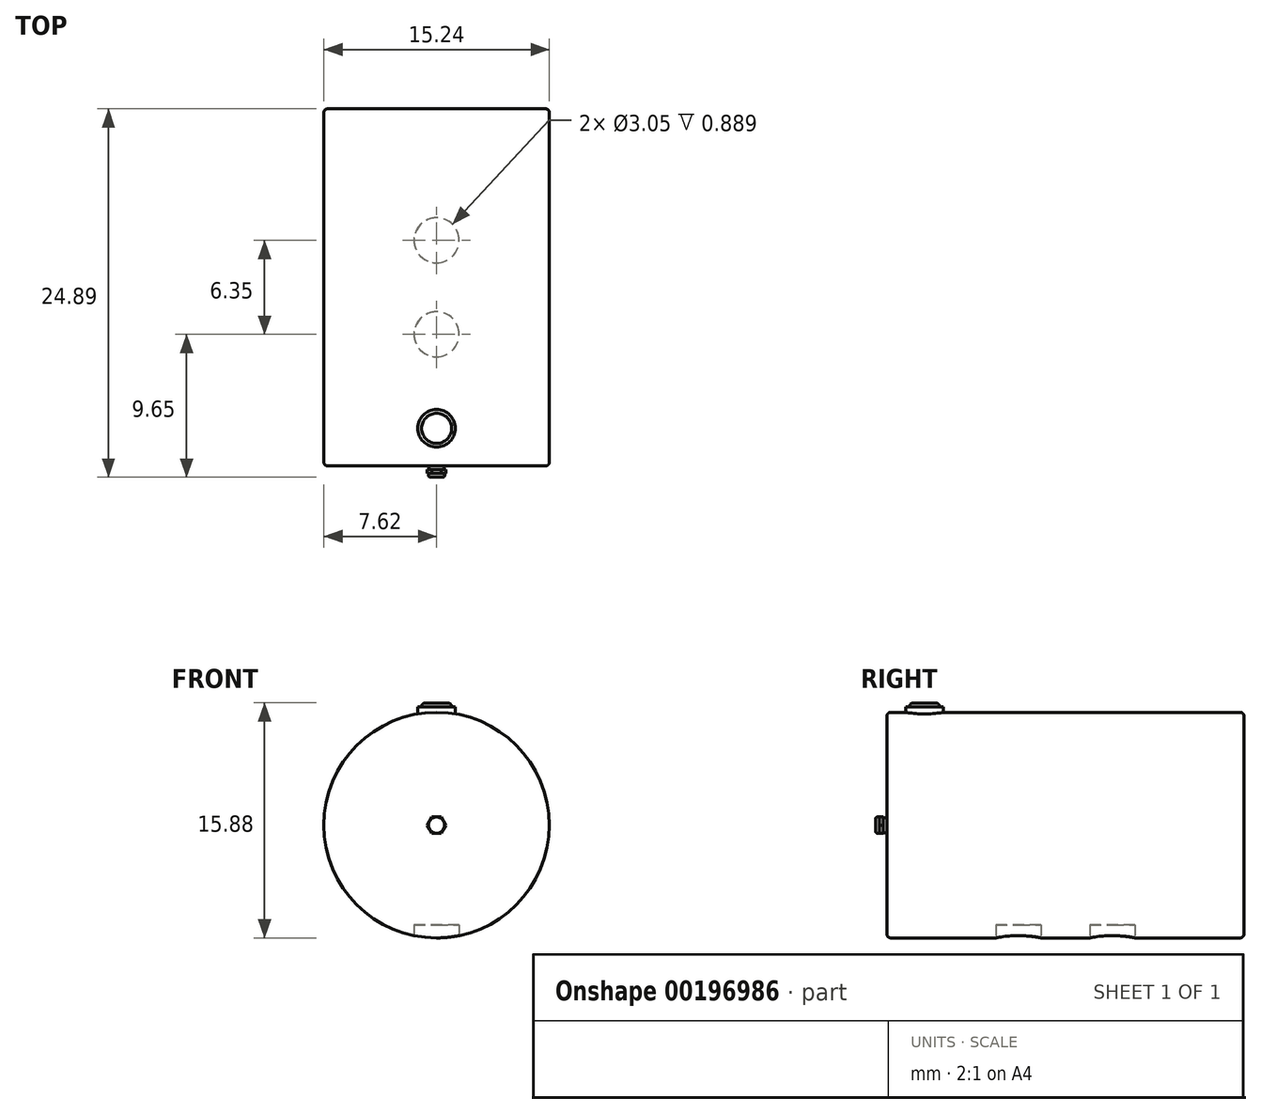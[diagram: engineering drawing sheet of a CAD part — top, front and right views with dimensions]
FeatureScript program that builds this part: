
annotation { "Feature Type Name" : "Feature", "Feature Type Description" : "" }
export const myFeature = defineFeature(function(context is Context, id is Id, definition is map)
    precondition{}
    {
        {
            var Q0;
            Q0=qCreatedBy(makeId("Front.planeOp"),FACE);
            var sketch = newSketch(context, id + "F0", { "sketchPlane" : qUnion([Q0])});
            skCircle(sketch, "E0", {"center": v(0, 0) * mm, "radius": 7.62 * mm});
            skSolve(sketch);
        }
        {
            var Q0;
            Q0 = qSketchRegion(id + "F0", true);
            extrude(context, id + "F1", {"entities" : qUnion([Q0]), "oppositeDirection" : true, "depth" : 24.13 * mm});
        }
        {
            var Q0;
            Q0=qCreatedBy(makeId("Top.planeOp"),FACE);
            cPlane(context, id + "F2", {"entities" : qUnion([Q0]), "cplaneType" : CPlaneType.OFFSET, "offset" : 7.62 * mm, "oppositeDirection" : true, "width" : 152.4 * mm, "height" : 152.4 * mm});
        }
        {
            var Q0;
            Q0=qCreatedBy(id+"F2.planeOp",FACE);
            var sketch = newSketch(context, id + "F3", { "sketchPlane" : qUnion([Q0])});
            skCircle(sketch, "E1", {"center": v(0, 8.9) * mm, "radius": 1.52 * mm});
            skCircle(sketch, "E2", {"center": v(0, 15.24) * mm, "radius": 1.52 * mm});
            skSolve(sketch);
        }
        {
            var Q0;
            Q0 = qSketchRegion(id + "F3", true);
            extrude(context, id + "F4", {"entities" : qUnion([Q0]), "operationType" : NewBodyOperationType.REMOVE, "depth" : 0.89 * mm});
        }
        {
            var Q0;
            Q0=makeQuery(id+"F1.opExtrude","CAP_FACE",FACE,{"disambiguationData":[OSD([sQuery(id+"F0.wireOp",EDGE,"E0")])],"isStart":true});
            var sketch = newSketch(context, id + "F5", { "sketchPlane" : qUnion([Q0])});
            skCircle(sketch, "E3", {"center": v(0, 0) * mm, "radius": 0.5 * mm});
            skSolve(sketch);
        }
        {
            var Q0;
            Q0 = qSketchRegion(id + "F5", true);
            extrude(context, id + "F6", {"entities" : qUnion([Q0]), "operationType" : NewBodyOperationType.ADD, "depth" : 0.25 * mm});
        }
        {
            var Q0;
            Q0=makeQuery(id+"F6.opExtrude","CAP_FACE",FACE,{"disambiguationData":[OSD([sQuery(id+"F5.wireOp",EDGE,"E3")])],"isStart":false});
            var sketch = newSketch(context, id + "F7", { "sketchPlane" : qUnion([Q0])});
            skCircle(sketch, "E4.cCircle", {"center": v(0, 0) * mm, "radius": 0.64 * mm, "construction": true});
            skLineSegment(sketch, "E4.0", {"start": v(-0.32, 0.55) * mm, "end": v(0.32, 0.55) * mm});
            skLineSegment(sketch, "E4.1", {"start": v(0.32, 0.55) * mm, "end": v(0.64, 0) * mm});
            skLineSegment(sketch, "E4.2", {"start": v(0.64, 0) * mm, "end": v(0.32, -0.55) * mm});
            skLineSegment(sketch, "E4.3", {"start": v(0.32, -0.55) * mm, "end": v(-0.32, -0.55) * mm});
            skLineSegment(sketch, "E4.4", {"start": v(-0.32, -0.55) * mm, "end": v(-0.63, 0) * mm});
            skLineSegment(sketch, "E4.5", {"start": v(-0.63, 0) * mm, "end": v(-0.32, 0.55) * mm});
            skSolve(sketch);
        }
        {
            var Q0;
            Q0 = qSketchRegion(id + "F7", true);
            extrude(context, id + "F8", {"entities" : qUnion([Q0]), "operationType" : NewBodyOperationType.ADD, "depth" : 0.25 * mm});
        }
        {
            var Q0;
            Q0=makeQuery(id+"F8.opExtrude","CAP_FACE",FACE,{"disambiguationData":[OSD([sQuery(id+"F7.wireOp",EDGE,"E4.0"),sQuery(id+"F7.wireOp",EDGE,"E4.1"),sQuery(id+"F7.wireOp",EDGE,"E4.2"),sQuery(id+"F7.wireOp",EDGE,"E4.3"),sQuery(id+"F7.wireOp",EDGE,"E4.4"),sQuery(id+"F7.wireOp",EDGE,"E4.5")])],"isStart":false});
            var sketch = newSketch(context, id + "F9", { "sketchPlane" : qUnion([Q0])});
            skCircle(sketch, "E5", {"center": v(0, 0) * mm, "radius": 0.55 * mm});
            skSolve(sketch);
        }
        {
            var Q0;
            Q0 = qSketchRegion(id + "F9", true);
            extrude(context, id + "F10", {"entities" : qUnion([Q0]), "operationType" : NewBodyOperationType.ADD, "depth" : 0.25 * mm});
        }
        {
            var Q0;
            Q0=makeQuery(id+"F6.opExtrude","CAP_EDGE",EDGE,{"disambiguationData":[OSD([sQuery(id+"F5.wireOp",EDGE,"E3")])],"isStart":true});
            var Q1;
            Q1=makeQuery(id+"F10.opExtrude","CAP_EDGE",EDGE,{"disambiguationData":[OSD([sQuery(id+"F9.wireOp",EDGE,"E5")])],"isStart":false});
            fillet(context, id + "F11", {"entities" : qUnion([Q0, Q1]), "radius" : 0.13 * mm, "tangentPropagation" : true, "allowEdgeOverflow" : false});
        }
        {
            var Q0;
            Q0=qCreatedBy(makeId("Top.planeOp"),FACE);
            cPlane(context, id + "F12", {"entities" : qUnion([Q0]), "cplaneType" : CPlaneType.OFFSET, "offset" : 7.62 * mm, "width" : 152.4 * mm, "height" : 152.4 * mm});
        }
        {
            var Q0;
            Q0=qCreatedBy(id+"F12.planeOp",FACE);
            var sketch = newSketch(context, id + "F13", { "sketchPlane" : qUnion([Q0])});
            skCircle(sketch, "E6", {"center": v(0, 2.54) * mm, "radius": 1.27 * mm});
            skSolve(sketch);
        }
        {
            var Q0;
            Q0 = qSketchRegion(id + "F13", true);
            extrude(context, id + "F14", {"entities" : qUnion([Q0]), "operationType" : NewBodyOperationType.ADD, "depth" : 0.38 * mm, "hasSecondDirection" : true, "secondDirectionOppositeDirection" : true, "secondDirectionDepth" : 0.25 * mm});
        }
        {
            var Q0;
            Q0=makeQuery(id+"F1.opExtrude","CAP_EDGE",EDGE,{"disambiguationData":[OSD([sQuery(id+"F0.wireOp",EDGE,"E0")])],"isStart":true});
            var Q1;
            Q1=makeQuery(id+"F1.opExtrude","CAP_EDGE",EDGE,{"disambiguationData":[OSD([sQuery(id+"F0.wireOp",EDGE,"E0")])],"isStart":false});
            fillet(context, id + "F15", {"entities" : qUnion([Q0, Q1]), "radius" : 0.25 * mm, "tangentPropagation" : true, "allowEdgeOverflow" : false});
        }
        {
            var Q0;
            Q0=makeQuery(id+"F14.opExtrude","CAP_FACE",FACE,{"disambiguationData":[OSD([sQuery(id+"F13.wireOp",EDGE,"E6")])],"isStart":false});
            var sketch = newSketch(context, id + "F16", { "sketchPlane" : qUnion([Q0])});
            skCircle(sketch, "E7", {"center": v(0, 2.54) * mm, "radius": 1.02 * mm});
            skSolve(sketch);
        }
        {
            var Q0;
            Q0 = qSketchRegion(id + "F16", true);
            extrude(context, id + "F17", {"entities" : qUnion([Q0]), "operationType" : NewBodyOperationType.ADD, "depth" : 0.25 * mm});
        }
        {
            var Q0;
            Q0=makeQuery(id+"F17.opExtrude","CAP_EDGE",EDGE,{"disambiguationData":[OSD([sQuery(id+"F16.wireOp",EDGE,"E7")])],"isStart":false});
            fillet(context, id + "F18", {"entities" : qUnion([Q0]), "radius" : 0.25 * mm, "tangentPropagation" : true, "allowEdgeOverflow" : false});
        }
    });
